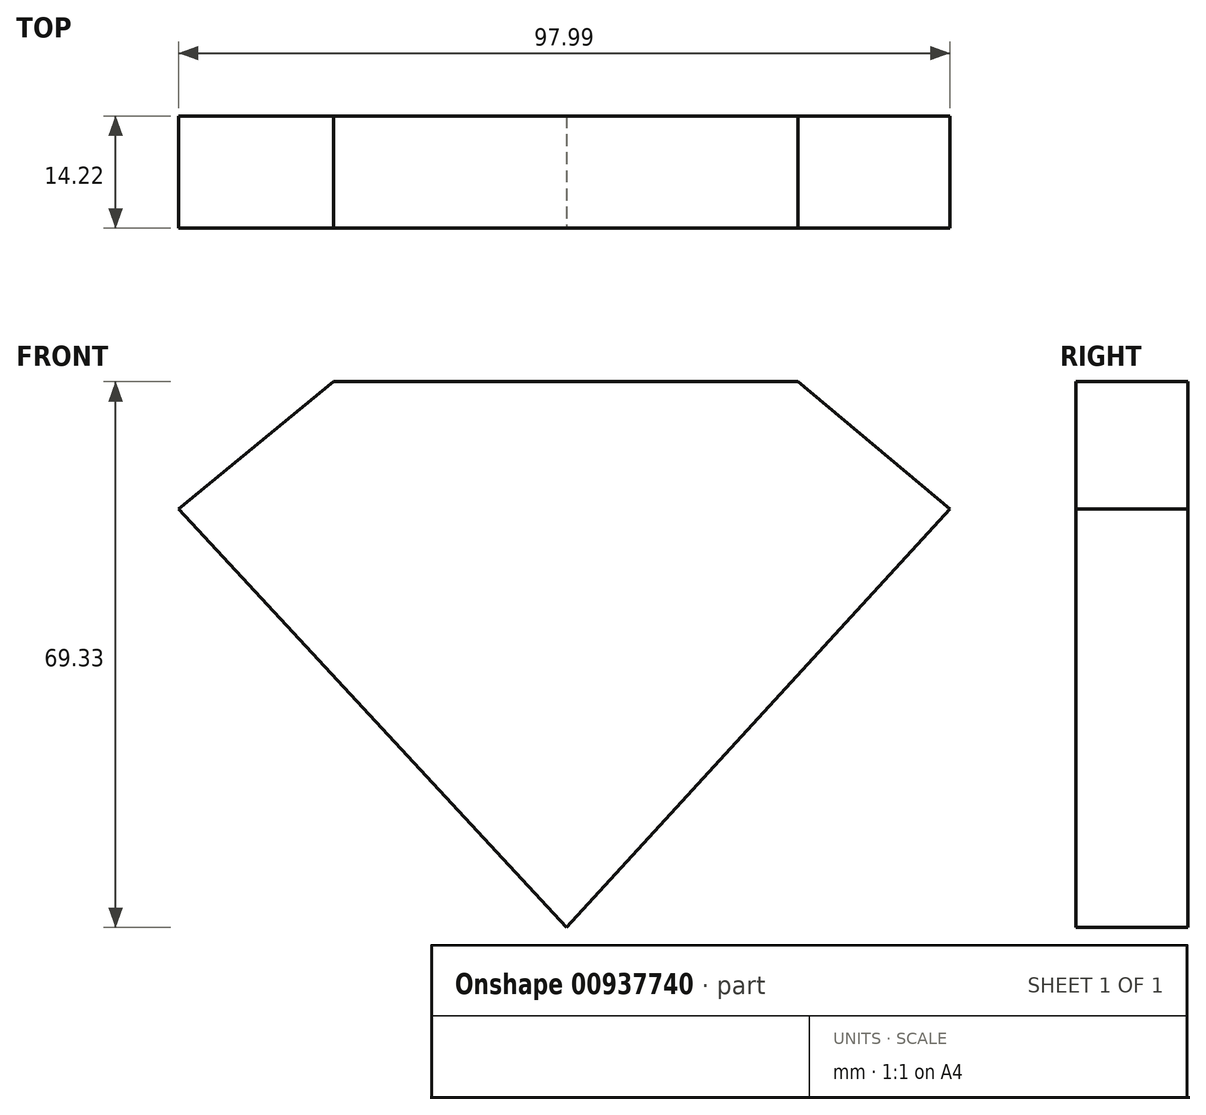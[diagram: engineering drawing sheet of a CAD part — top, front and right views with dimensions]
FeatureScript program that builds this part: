
annotation { "Feature Type Name" : "Feature", "Feature Type Description" : "" }
export const myFeature = defineFeature(function(context is Context, id is Id, definition is map)
    precondition{}
    {
        {
            var Q0;
            Q0=qCreatedBy(makeId("Front.planeOp"),FACE);
            var sketch = newSketch(context, id + "F0", { "sketchPlane" : qUnion([Q0])});
            skLineSegment(sketch, "E0", {"start": v(0, -39.72) * mm, "end": v(-49.3, 13.7) * mm});
            skLineSegment(sketch, "E1", {"start": v(-49.3, 13.7) * mm, "end": v(-29.62, 29.89) * mm});
            skLineSegment(sketch, "E2", {"start": v(-29.62, 29.89) * mm, "end": v(29.12, 29.89) * mm});
            skLineSegment(sketch, "E3", {"start": v(29.12, 29.89) * mm, "end": v(48.7, 13.76) * mm});
            skLineSegment(sketch, "E4", {"start": v(48.7, 13.76) * mm, "end": v(0, -39.72) * mm});
            skLineSegment(sketch, "E5", {"start": v(14.9, 21.95) * mm, "end": v(19.07, 18.34) * mm});
            skLineSegment(sketch, "E6", {"start": v(19.07, 18.34) * mm, "end": v(19.7, 21.91) * mm});
            skLineSegment(sketch, "E7", {"start": v(19.7, 21.91) * mm, "end": v(14.9, 21.95) * mm});
            skLineSegment(sketch, "E8", {"start": v(19.84, 16.2) * mm, "end": v(20.8, 22.94) * mm});
            skLineSegment(sketch, "E9", {"start": v(20.8, 22.94) * mm, "end": v(10.7, 22.94) * mm});
            skLineSegment(sketch, "E10", {"start": v(10.7, 22.94) * mm, "end": v(10.7, 22.72) * mm});
            skArc(sketch, "E11", {"start": v(17.64, 18.42) * mm, "mid": v(14.45, 21.02) * mm, "end": v(10.7, 22.72) * mm});
            skLineSegment(sketch, "E12", {"start": v(17.64, 18.42) * mm, "end": v(19.84, 16.2) * mm});
            skLineSegment(sketch, "E13", {"start": v(-38.3, 13.38) * mm, "end": v(-26.9, 23) * mm});
            skLineSegment(sketch, "E14", {"start": v(-26.9, 23) * mm, "end": v(-17.35, 23) * mm});
            skLineSegment(sketch, "E15", {"start": v(-17.35, 23) * mm, "end": v(-17.35, 22.83) * mm});
            skArc(sketch, "E16", {"start": v(-17.35, 22.83) * mm, "mid": v(-21.65, 21.09) * mm, "end": v(-25.56, 18.6) * mm});
            skArc(sketch, "E17", {"start": v(-25.56, 18.6) * mm, "mid": v(-28.82, 15.54) * mm, "end": v(-30.77, 11.5) * mm});
            skArc(sketch, "E18", {"start": v(-30.77, 11.5) * mm, "mid": v(-31.25, 8.58) * mm, "end": v(-31, 5.62) * mm});
            skLineSegment(sketch, "E19", {"start": v(-38.3, 13.38) * mm, "end": v(-31, 5.62) * mm});
            skArc(sketch, "E20", {"start": v(-25.94, 19.53) * mm, "mid": v(-30.4, 14.64) * mm, "end": v(-32.16, 8.26) * mm});
            skLineSegment(sketch, "E21", {"start": v(-25.94, 19.53) * mm, "end": v(-21.73, 21.95) * mm});
            skLineSegment(sketch, "E22", {"start": v(-21.73, 21.95) * mm, "end": v(-26.6, 21.95) * mm});
            skLineSegment(sketch, "E23", {"start": v(-26.6, 21.95) * mm, "end": v(-36.89, 13.27) * mm});
            skLineSegment(sketch, "E24", {"start": v(-36.89, 13.27) * mm, "end": v(-32.16, 8.26) * mm});
            skArc(sketch, "E25", {"start": v(26.96, 3.37) * mm, "mid": v(22.48, 7.33) * mm, "end": v(16.93, 9.53) * mm});
            skArc(sketch, "E26", {"start": v(16.93, 9.53) * mm, "mid": v(10.46, 10.28) * mm, "end": v(3.95, 10.5) * mm});
            skArc(sketch, "E27", {"start": v(-5.93, 10.8) * mm, "mid": v(-1, 10.54) * mm, "end": v(3.95, 10.5) * mm});
            skArc(sketch, "E28", {"start": v(-12.67, 11.7) * mm, "mid": v(-9.34, 10.97) * mm, "end": v(-5.93, 10.8) * mm});
            skArc(sketch, "E29", {"start": v(-16.5, 13.44) * mm, "mid": v(-14.67, 12.38) * mm, "end": v(-12.67, 11.7) * mm});
            skArc(sketch, "E30", {"start": v(-15.77, 18.56) * mm, "mid": v(-17.53, 16.2) * mm, "end": v(-16.5, 13.44) * mm});
            skArc(sketch, "E31", {"start": v(1.08, 21.89) * mm, "mid": v(-7.68, 21.93) * mm, "end": v(-15.77, 18.56) * mm});
            skArc(sketch, "E32", {"start": v(10.38, 18.36) * mm, "mid": v(5.98, 20.8) * mm, "end": v(1.08, 21.89) * mm});
            skArc(sketch, "E33", {"start": v(13.79, 11.93) * mm, "mid": v(12.73, 15.49) * mm, "end": v(10.38, 18.36) * mm});
            skLineSegment(sketch, "E34", {"start": v(13.79, 11.93) * mm, "end": v(28.82, 11.93) * mm});
            skLineSegment(sketch, "E35", {"start": v(28.82, 11.93) * mm, "end": v(28.82, 19.33) * mm});
            skLineSegment(sketch, "E36", {"start": v(28.82, 19.33) * mm, "end": v(35.99, 13.2) * mm});
            skLineSegment(sketch, "E37", {"start": v(35.99, 13.2) * mm, "end": v(26.96, 3.37) * mm});
            skArc(sketch, "E38", {"start": v(14.68, 12.9) * mm, "mid": v(12.56, 17.6) * mm, "end": v(8.44, 20.73) * mm});
            skArc(sketch, "E39", {"start": v(8.44, 20.73) * mm, "mid": v(3.1, 22.6) * mm, "end": v(-2.52, 23.13) * mm});
            skArc(sketch, "E40", {"start": v(-2.52, 23.13) * mm, "mid": v(-5.71, 23.1) * mm, "end": v(-8.87, 22.66) * mm});
            skArc(sketch, "E41", {"start": v(-8.87, 22.66) * mm, "mid": v(-12.56, 21.47) * mm, "end": v(-16, 19.68) * mm});
            skArc(sketch, "E42", {"start": v(-16, 19.68) * mm, "mid": v(-18.17, 17.33) * mm, "end": v(-18.17, 14.14) * mm});
            skArc(sketch, "E43", {"start": v(-18.17, 14.14) * mm, "mid": v(-15.95, 11.9) * mm, "end": v(-12.98, 10.85) * mm});
            skArc(sketch, "E44", {"start": v(-12.98, 10.85) * mm, "mid": v(-9.02, 9.96) * mm, "end": v(-4.96, 9.68) * mm});
            skLineSegment(sketch, "E45", {"start": v(-4.96, 9.68) * mm, "end": v(12, 9.14) * mm});
            skArc(sketch, "E46", {"start": v(25.26, 3.8) * mm, "mid": v(19.22, 7.92) * mm, "end": v(12, 9.14) * mm});
            skLineSegment(sketch, "E47", {"start": v(25.26, 3.8) * mm, "end": v(26.92, 2.04) * mm});
            skLineSegment(sketch, "E48", {"start": v(26.92, 2.04) * mm, "end": v(37.5, 13.2) * mm});
            skLineSegment(sketch, "E49", {"start": v(37.5, 13.2) * mm, "end": v(28, 21.35) * mm});
            skLineSegment(sketch, "E50", {"start": v(28, 21.35) * mm, "end": v(28, 12.86) * mm});
            skLineSegment(sketch, "E51", {"start": v(28, 12.86) * mm, "end": v(14.68, 12.9) * mm});
            skArc(sketch, "E52", {"start": v(16.46, -6.74) * mm, "mid": v(16.93, -5.8) * mm, "end": v(16.3, -4.96) * mm});
            skArc(sketch, "E53", {"start": v(16.3, -4.96) * mm, "mid": v(13.39, -3.56) * mm, "end": v(10.19, -3.1) * mm});
            skArc(sketch, "E54", {"start": v(11.81, -9.14) * mm, "mid": v(14.26, -8.18) * mm, "end": v(16.46, -6.74) * mm});
            skArc(sketch, "E55", {"start": v(8.64, -9.76) * mm, "mid": v(10.26, -9.65) * mm, "end": v(11.81, -9.14) * mm});
            skLineSegment(sketch, "E56", {"start": v(8.64, -9.76) * mm, "end": v(-1.05, -9.76) * mm});
            skArc(sketch, "E57", {"start": v(-1.05, -9.76) * mm, "mid": v(-5.3, -6.29) * mm, "end": v(-10.66, -5.04) * mm});
            skArc(sketch, "E58", {"start": v(-10.66, -4.96) * mm, "mid": v(-14.75, -5.62) * mm, "end": v(-18.64, -7.05) * mm});
            skLineSegment(sketch, "E59", {"start": v(-18.64, -7.05) * mm, "end": v(-24.37, -0.54) * mm});
            skArc(sketch, "E60", {"start": v(-24.37, -0.54) * mm, "mid": v(-15.93, -1.9) * mm, "end": v(-7.4, -2.56) * mm});
            skArc(sketch, "E61", {"start": v(-7.4, -2.56) * mm, "mid": v(-1.4, -2.8) * mm, "end": v(4.6, -2.68) * mm});
            skArc(sketch, "E62", {"start": v(10.19, -3.1) * mm, "mid": v(7.4, -2.82) * mm, "end": v(4.6, -2.68) * mm});
            skArc(sketch, "E63", {"start": v(-1.75, -10.7) * mm, "mid": v(-5.47, -7.12) * mm, "end": v(-10.5, -5.97) * mm});
            skArc(sketch, "E64", {"start": v(-10.5, -5.97) * mm, "mid": v(-14.5, -6.53) * mm, "end": v(-18.25, -8.06) * mm});
            skArc(sketch, "E65", {"start": v(-18.61, -8.21) * mm, "mid": v(-18.43, -8.14) * mm, "end": v(-18.25, -8.06) * mm});
            skLineSegment(sketch, "E66", {"start": v(-18.61, -8.21) * mm, "end": v(-27.57, 1.58) * mm});
            skArc(sketch, "E67", {"start": v(-27.57, 1.58) * mm, "mid": v(-22.52, 0.22) * mm, "end": v(-17.37, -0.67) * mm});
            skArc(sketch, "E68", {"start": v(-17.37, -0.67) * mm, "mid": v(-13.6, -1.17) * mm, "end": v(-9.82, -1.32) * mm});
            skArc(sketch, "E69", {"start": v(8.3, -1.9) * mm, "mid": v(-0.76, -1.6) * mm, "end": v(-9.82, -1.32) * mm});
            skArc(sketch, "E70", {"start": v(12.04, -2.23) * mm, "mid": v(10.18, -1.97) * mm, "end": v(8.3, -1.9) * mm});
            skArc(sketch, "E71", {"start": v(16.18, -3.53) * mm, "mid": v(14.17, -2.7) * mm, "end": v(12.04, -2.23) * mm});
            skArc(sketch, "E72", {"start": v(18.07, -5.81) * mm, "mid": v(17.34, -4.5) * mm, "end": v(16.18, -3.53) * mm});
            skArc(sketch, "E73", {"start": v(15.82, -8.55) * mm, "mid": v(17.32, -7.49) * mm, "end": v(18.07, -5.81) * mm});
            skArc(sketch, "E74", {"start": v(8.5, -10.67) * mm, "mid": v(12.27, -9.99) * mm, "end": v(15.82, -8.55) * mm});
            skLineSegment(sketch, "E75", {"start": v(-1.75, -10.7) * mm, "end": v(8.5, -10.67) * mm});
            skArc(sketch, "E76", {"start": v(-11.64, -15.03) * mm, "mid": v(-0.2, -15.86) * mm, "end": v(11.23, -14.97) * mm});
            skLineSegment(sketch, "E77", {"start": v(11.23, -14.97) * mm, "end": v(0, -27.3) * mm});
            skLineSegment(sketch, "E78", {"start": v(0, -27.3) * mm, "end": v(-11.64, -15.03) * mm});
            skArc(sketch, "E79", {"start": v(-9.06, -16.4) * mm, "mid": v(-0.26, -16.88) * mm, "end": v(8.53, -16.4) * mm});
            skLineSegment(sketch, "E80", {"start": v(-9.06, -16.4) * mm, "end": v(-0.28, -25.67) * mm});
            skLineSegment(sketch, "E81", {"start": v(-0.28, -25.67) * mm, "end": v(8.53, -16.4) * mm});
            skSolve(sketch);
        }
        {
            var Q0;
            Q0=sQuery(id+"F0.wireOp",EDGE,"E74");
            var Q1;
            Q1=sQuery(id+"F0.wireOp",EDGE,"E71");
            var Q2;
            Q2=sQuery(id+"F0.wireOp",EDGE,"E49");
            var Q3;
            Q3=sQuery(id+"F0.wireOp",EDGE,"E29");
            var Q4;
            Q4=sQuery(id+"F0.wireOp",EDGE,"E40");
            var Q5;
            Q5=sQuery(id+"F0.wireOp",EDGE,"E69");
            var Q6;
            Q6=sQuery(id+"F0.wireOp",EDGE,"E41");
            var Q7;
            Q7=sQuery(id+"F0.wireOp",EDGE,"E44");
            var Q8;
            Q8=sQuery(id+"F0.wireOp",EDGE,"E66");
            var Q9;
            Q9=sQuery(id+"F0.wireOp",EDGE,"E13");
            var Q10;
            Q10=sQuery(id+"F0.wireOp",EDGE,"E63");
            var Q11;
            Q11=sQuery(id+"F0.wireOp",EDGE,"E25");
            var Q12;
            Q12=sQuery(id+"F0.wireOp",EDGE,"E58");
            var Q13;
            Q13=sQuery(id+"F0.wireOp",EDGE,"E60");
            var Q14;
            Q14=sQuery(id+"F0.wireOp",EDGE,"E1");
            var Q15;
            Q15=sQuery(id+"F0.wireOp",EDGE,"E68");
            var Q16;
            Q16=sQuery(id+"F0.wireOp",EDGE,"E0");
            var Q17;
            Q17=sQuery(id+"F0.wireOp",EDGE,"E57");
            var Q18;
            Q18=sQuery(id+"F0.wireOp",EDGE,"E4");
            var Q19;
            Q19=sQuery(id+"F0.wireOp",EDGE,"E22");
            var Q20;
            Q20=sQuery(id+"F0.wireOp",EDGE,"E78");
            var Q21;
            Q21=sQuery(id+"F0.wireOp",EDGE,"E27");
            var Q22;
            Q22=sQuery(id+"F0.wireOp",EDGE,"E56");
            var Q23;
            Q23=sQuery(id+"F0.wireOp",EDGE,"E42");
            var Q24;
            Q24=sQuery(id+"F0.wireOp",EDGE,"E62");
            var Q25;
            Q25=sQuery(id+"F0.wireOp",EDGE,"E17");
            var Q26;
            Q26=sQuery(id+"F0.wireOp",EDGE,"E34");
            var Q27;
            Q27=sQuery(id+"F0.wireOp",EDGE,"E16");
            var Q28;
            Q28=sQuery(id+"F0.wireOp",EDGE,"E75");
            var Q29;
            Q29=sQuery(id+"F0.wireOp",EDGE,"E24");
            var Q30;
            Q30=sQuery(id+"F0.wireOp",EDGE,"E33");
            var Q31;
            Q31=sQuery(id+"F0.wireOp",EDGE,"E51");
            var Q32;
            Q32=sQuery(id+"F0.wireOp",EDGE,"E5");
            var Q33;
            Q33=sQuery(id+"F0.wireOp",EDGE,"E79");
            var Q34;
            Q34=sQuery(id+"F0.wireOp",EDGE,"E61");
            var Q35;
            Q35=sQuery(id+"F0.wireOp",EDGE,"E77");
            var Q36;
            Q36=sQuery(id+"F0.wireOp",EDGE,"E23");
            var Q37;
            Q37=sQuery(id+"F0.wireOp",EDGE,"E6");
            var Q38;
            Q38=sQuery(id+"F0.wireOp",EDGE,"E9");
            var Q39;
            Q39=sQuery(id+"F0.wireOp",EDGE,"E80");
            var Q40;
            Q40=sQuery(id+"F0.wireOp",EDGE,"E46");
            var Q41;
            Q41=sQuery(id+"F0.wireOp",EDGE,"E3");
            var Q42;
            Q42=sQuery(id+"F0.wireOp",EDGE,"E31");
            var Q43;
            Q43=sQuery(id+"F0.wireOp",EDGE,"E19");
            var Q44;
            Q44=sQuery(id+"F0.wireOp",EDGE,"E26");
            var Q45;
            Q45=sQuery(id+"F0.wireOp",EDGE,"E7");
            var Q46;
            Q46=sQuery(id+"F0.wireOp",EDGE,"E30");
            var Q47;
            Q47=sQuery(id+"F0.wireOp",EDGE,"E20");
            var Q48;
            Q48=sQuery(id+"F0.wireOp",EDGE,"E11");
            var Q49;
            Q49=sQuery(id+"F0.wireOp",EDGE,"E36");
            var Q50;
            Q50=sQuery(id+"F0.wireOp",EDGE,"E37");
            var Q51;
            Q51=sQuery(id+"F0.wireOp",EDGE,"E35");
            var Q52;
            Q52=sQuery(id+"F0.wireOp",EDGE,"E76");
            var Q53;
            Q53=sQuery(id+"F0.wireOp",EDGE,"E64");
            var Q54;
            Q54=sQuery(id+"F0.wireOp",EDGE,"E8");
            var Q55;
            Q55=sQuery(id+"F0.wireOp",EDGE,"E45");
            var Q56;
            Q56=sQuery(id+"F0.wireOp",EDGE,"E48");
            var Q57;
            Q57=sQuery(id+"F0.wireOp",EDGE,"E14");
            var Q58;
            Q58=sQuery(id+"F0.wireOp",EDGE,"E43");
            var Q59;
            Q59=sQuery(id+"F0.wireOp",EDGE,"E50");
            var Q60;
            Q60=sQuery(id+"F0.wireOp",EDGE,"E39");
            var Q61;
            Q61=sQuery(id+"F0.wireOp",EDGE,"E53");
            var Q62;
            Q62=sQuery(id+"F0.wireOp",EDGE,"E32");
            var Q63;
            Q63=sQuery(id+"F0.wireOp",EDGE,"E21");
            var Q64;
            Q64=sQuery(id+"F0.wireOp",EDGE,"E38");
            var Q65;
            Q65=sQuery(id+"F0.wireOp",EDGE,"E2");
            var Q66;
            Q66=sQuery(id+"F0.wireOp",EDGE,"E28");
            var Q67;
            Q67=sQuery(id+"F0.wireOp",EDGE,"E81");
            var Q68;
            Q68=sQuery(id+"F0.wireOp",EDGE,"E59");
            var Q69;
            Q69=sQuery(id+"F0.wireOp",EDGE,"E67");
            var Q70;
            Q70=sQuery(id+"F0.wireOp",EDGE,"E54");
            var Q71;
            Q71=sQuery(id+"F0.wireOp",EDGE,"E55");
            var Q72;
            Q72=sQuery(id+"F0.wireOp",EDGE,"E70");
            var Q73;
            Q73=sQuery(id+"F0.wireOp",EDGE,"E73");
            var Q74;
            Q74=sQuery(id+"F0.wireOp",EDGE,"E72");
            var Q75;
            Q75=sQuery(id+"F0.wireOp",EDGE,"E12");
            var Q76;
            Q76=sQuery(id+"F0.wireOp",EDGE,"E47");
            var Q77;
            Q77=sQuery(id+"F0.wireOp",EDGE,"E10");
            var Q78;
            Q78=sQuery(id+"F0.wireOp",EDGE,"E18");
            var Q79;
            Q79=sQuery(id+"F0.wireOp",EDGE,"E52");
            var Q80;
            Q80=sQuery(id+"F0.wireOp",EDGE,"E65");
            var Q81;
            Q81=sQuery(id+"F0.wireOp",EDGE,"E15");
            extrude(context, id + "F1", {"bodyType" : ToolBodyType.SURFACE, "surfaceEntities" : qUnion([Q0, Q1, Q2, Q3, Q4, Q5, Q6, Q7, Q8, Q9, Q10, Q11, Q12, Q13, Q14, Q15, Q16, Q17, Q18, Q19, Q20, Q21, Q22, Q23, Q24, Q25, Q26, Q27, Q28, Q29, Q30, Q31, Q32, Q33, Q34, Q35, Q36, Q37, Q38, Q39, Q40, Q41, Q42, Q43, Q44, Q45, Q46, Q47, Q48, Q49, Q50, Q51, Q52, Q53, Q54, Q55, Q56, Q57, Q58, Q59, Q60, Q61, Q62, Q63, Q64, Q65, Q66, Q67, Q68, Q69, Q70, Q71, Q72, Q73, Q74, Q75, Q76, Q77, Q78, Q79, Q80, Q81]), "endBound" : BoundingType.SYMMETRIC, "depth" : 25.4 * mm, "offsetDistance" : 25.4 * mm});
        }
        {
            var Q0;
            Q0=qCreatedBy(makeId("Front.planeOp"),FACE);
            var sketch = newSketch(context, id + "F2", { "sketchPlane" : qUnion([Q0])});
            skLineSegment(sketch, "E82", {"start": v(-29.65, 30.04) * mm, "end": v(29.38, 30.04) * mm});
            skLineSegment(sketch, "E83", {"start": v(29.38, 30.04) * mm, "end": v(48.67, 13.88) * mm});
            skLineSegment(sketch, "E84", {"start": v(48.67, 13.88) * mm, "end": v(0, -39.29) * mm});
            skLineSegment(sketch, "E85", {"start": v(0, -39.29) * mm, "end": v(-49.32, 13.88) * mm});
            skLineSegment(sketch, "E86", {"start": v(-49.32, 13.88) * mm, "end": v(-29.65, 30.04) * mm});
            skSolve(sketch);
        }
        {
            var Q0;
            Q0 = qSketchRegion(id + "F2", true);
            extrude(context, id + "F3", {"entities" : qUnion([Q0]), "oppositeDirection" : true, "depth" : 14.22 * mm, "offsetDistance" : 25.4 * mm});
        }
    });
